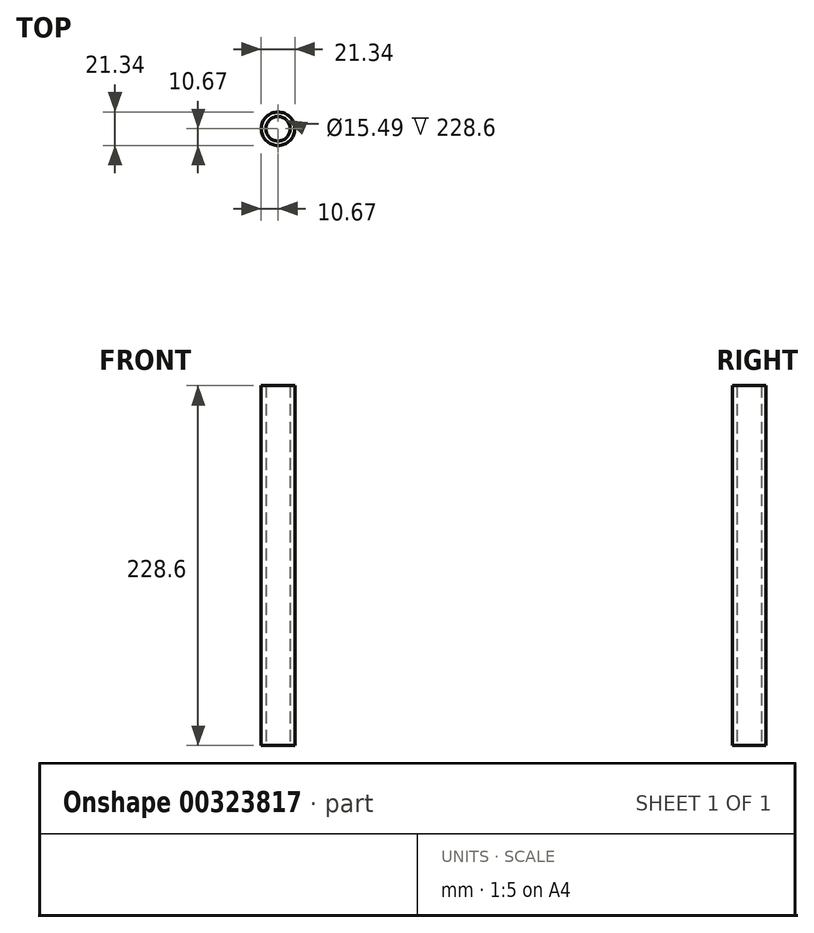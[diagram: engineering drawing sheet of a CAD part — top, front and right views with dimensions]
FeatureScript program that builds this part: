
annotation { "Feature Type Name" : "Feature", "Feature Type Description" : "" }
export const myFeature = defineFeature(function(context is Context, id is Id, definition is map)
    precondition{}
    {
        {
            var Q0;
            Q0=qCreatedBy(makeId("Top.planeOp"),FACE);
            var sketch = newSketch(context, id + "F0", { "sketchPlane" : qUnion([Q0])});
            skCircle(sketch, "E0", {"center": v(0, 0) * mm, "radius": 7.75 * mm});
            skCircle(sketch, "E1", {"center": v(0, 0) * mm, "radius": 10.67 * mm});
            skSolve(sketch);
        }
        {
            var Q0;
            Q0=makeQuery(id+"F0.imprint","IMPRINT",FACE,{"disambiguationData":[TD([[makeQuery(id+"F0.imprint","IMPRINT",EDGE,{"derivedFrom":sQuery(id+"F0.wireOp",EDGE,"E0")}),-1.0]])]});
            extrude(context, id + "F1", {"entities" : qUnion([Q0]), "depth" : 228.6 * mm});
        }
    });
